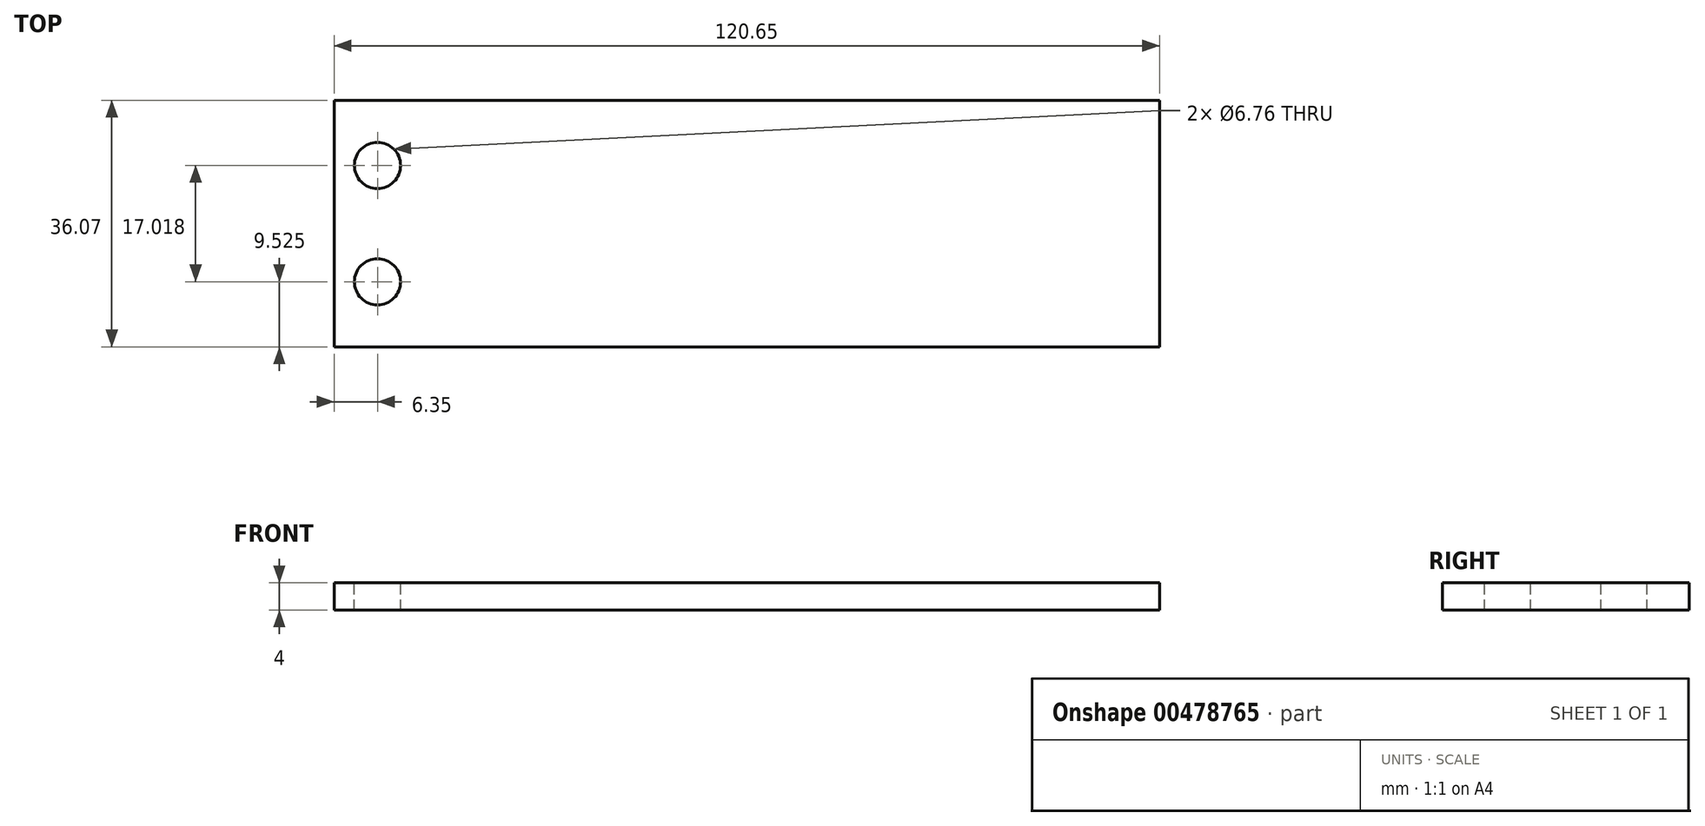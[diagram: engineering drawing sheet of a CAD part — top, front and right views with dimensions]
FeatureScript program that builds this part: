
annotation { "Feature Type Name" : "Feature", "Feature Type Description" : "" }
export const myFeature = defineFeature(function(context is Context, id is Id, definition is map)
    precondition{}
    {
        {
            var Q0;
            Q0=qCreatedBy(makeId("Right.planeOp"),FACE);
            var sketch = newSketch(context, id + "F0", { "sketchPlane" : qUnion([Q0])});
            skLineSegment(sketch, "E0.bottom", {"start": v(0, 0) * mm, "end": v(36.07, 0) * mm});
            skLineSegment(sketch, "E0.top", {"start": v(0, 4) * mm, "end": v(36.07, 4) * mm});
            skLineSegment(sketch, "E0.left", {"start": v(0, 0) * mm, "end": v(0, 4) * mm});
            skLineSegment(sketch, "E0.right", {"start": v(36.07, 0) * mm, "end": v(36.07, 4) * mm});
            skSolve(sketch);
        }
        {
            var Q0;
            Q0=makeQuery(id+"F0.imprint","IMPRINT",FACE,{"disambiguationData":[TD([[makeQuery(id+"F0.imprint","IMPRINT",EDGE,{"derivedFrom":sQuery(id+"F0.wireOp",EDGE,"E0.bottom")}),1.0]])]});
            extrude(context, id + "F1", {"entities" : qUnion([Q0]), "oppositeDirection" : true, "depth" : 120.65 * mm});
        }
        {
            var Q0;
            Q0=makeQuery(id+"F1.opExtrude","SWEPT_FACE",FACE,{"disambiguationData":[OSD([sQuery(id+"F0.wireOp",EDGE,"E0.top")])]});
            var sketch = newSketch(context, id + "F2", { "sketchPlane" : qUnion([Q0])});
            skSolve(sketch);
        }
        {
            var Q0;
            {var subQ0=sQuery(id+"F0.wireOp",EDGE,"E0.top");Q0=makeQuery(id+"F2.imprint","IMPRINT",FACE,{"disambiguationData":[TD([[makeQuery(id+"F2.imprint","IMPRINT",EDGE,{"derivedFrom":makeQuery(id+"F1.opExtrude","CAP_EDGE",EDGE,{"disambiguationData":[OSD([subQ0])],"isStart":true})}),1.0]])]});}
            var sketch = newSketch(context, id + "F3", { "sketchPlane" : qUnion([Q0])});
            skPoint(sketch, "E1", {"position": v(-114.3, 26.54) * mm});
            skPoint(sketch, "E2", {"position": v(-114.3, 9.52) * mm});
            skSolve(sketch);
        }
        {
            var Q0;
            Q0=sQuery(id+"F3.wireOp",VERTEX,"E1");
            var Q1;
            Q1=sQuery(id+"F3.wireOp",VERTEX,"E2");
            var Q2;
            Q2=makeQuery(id+"F1.opExtrude","SWEPT_BODY",BODY,{"disambiguationData":[OSD([sQuery(id+"F0.wireOp",EDGE,"E0.bottom"),sQuery(id+"F0.wireOp",EDGE,"E0.top"),sQuery(id+"F0.wireOp",EDGE,"E0.left"),sQuery(id+"F0.wireOp",EDGE,"E0.right")])]});
            hole(context, id + "F4", {"style" : HoleStyle.SIMPLE, "endStyle" : HoleEndStyle.THROUGH, "standardTappedOrClearance" : lookupTablePath({ "standard" : "ANSI", "fit" : "Normal (ASME)", "size" : "1/4", "type" : "Clearance" }), "standardBlindInLast" : lookupTablePath({ "fit" : "Free", "standard" : "ANSI", "size" : "1/4", "type" : "Clearance" }), "holeDiameter" : 6.76 * mm, "isTappedThrough" : true, "tappedDepth" : 12.7 * mm, "tapClearance" : 3, "locations" : qUnion([Q0, Q1]), "scope" : qUnion([Q2])});
        }
    });
